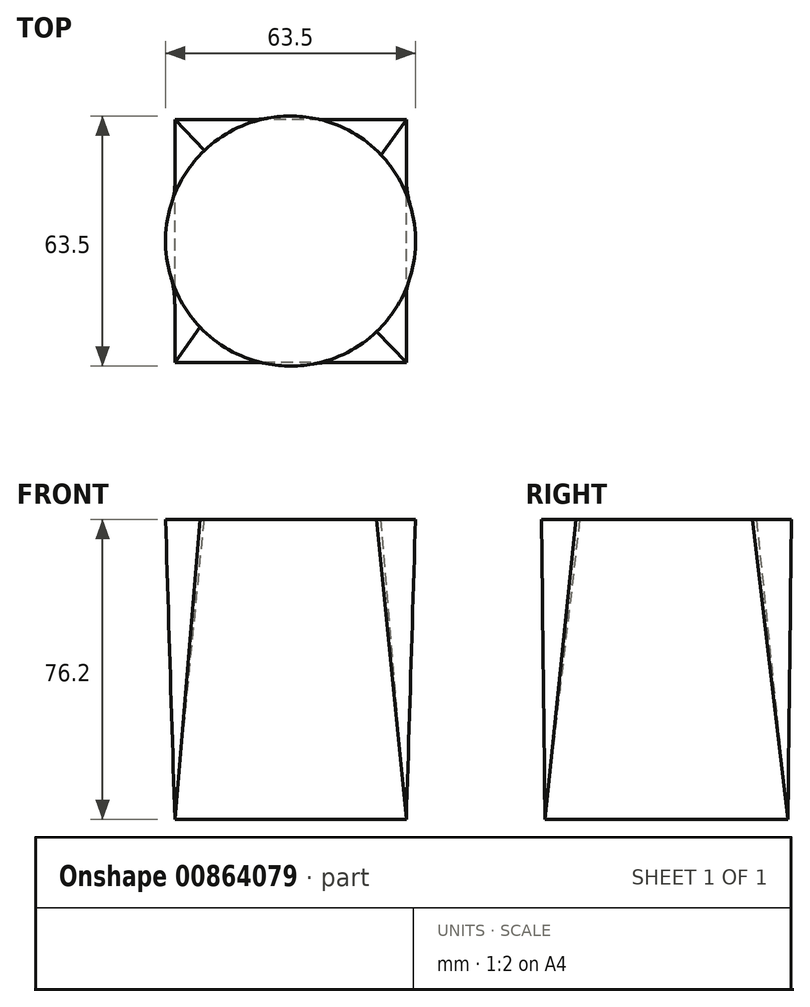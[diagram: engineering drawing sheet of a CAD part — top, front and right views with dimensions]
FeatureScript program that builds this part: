
annotation { "Feature Type Name" : "Feature", "Feature Type Description" : "" }
export const myFeature = defineFeature(function(context is Context, id is Id, definition is map)
    precondition{}
    {
        {
            var Q0;
            Q0=qCreatedBy(makeId("Top.planeOp"),FACE);
            var sketch = newSketch(context, id + "F0", { "sketchPlane" : qUnion([Q0])});
            skLineSegment(sketch, "E0.bottom", {"start": v(29.4, -30.85) * mm, "end": v(-29.4, -30.85) * mm});
            skLineSegment(sketch, "E0.top", {"start": v(29.4, 30.85) * mm, "end": v(-29.4, 30.85) * mm});
            skLineSegment(sketch, "E0.left", {"start": v(29.4, -30.85) * mm, "end": v(29.4, 30.85) * mm});
            skLineSegment(sketch, "E0.right", {"start": v(-29.4, -30.85) * mm, "end": v(-29.4, 30.85) * mm});
            skPoint(sketch, "E0.middle", {"position": v(0, 0) * mm});
            skSolve(sketch);
        }
        {
            var Q0;
            Q0=qCreatedBy(makeId("Top.planeOp"),FACE);
            cPlane(context, id + "F1", {"entities" : qUnion([Q0]), "cplaneType" : CPlaneType.OFFSET, "offset" : 76.2 * mm, "width" : 152.4 * mm, "height" : 152.4 * mm});
        }
        {
            var Q0;
            Q0=qCreatedBy(id+"F1.planeOp",FACE);
            var sketch = newSketch(context, id + "F2", { "sketchPlane" : qUnion([Q0])});
            skCircle(sketch, "E1", {"center": v(0, 0) * mm, "radius": 31.75 * mm});
            skSolve(sketch);
        }
        {
            var Q0;
            Q0=makeQuery(id+"F0.imprint","IMPRINT",FACE,{"disambiguationData":[TD([[makeQuery(id+"F0.imprint","IMPRINT",EDGE,{"derivedFrom":sQuery(id+"F0.wireOp",EDGE,"E0.bottom")}),-1.0]])]});
            var Q1;
            Q1=makeQuery(id+"F2.imprint","IMPRINT",FACE,{"disambiguationData":[TD([[makeQuery(id+"F2.imprint","IMPRINT",EDGE,{"derivedFrom":sQuery(id+"F2.wireOp",EDGE,"E1")}),1.0]])]});
            loft(context, id + "F3", {"sheetProfilesArray" : [{ "sheetProfileEntities" : qUnion([Q0]) }, { "sheetProfileEntities" : qUnion([Q1]) }]});
        }
    });
